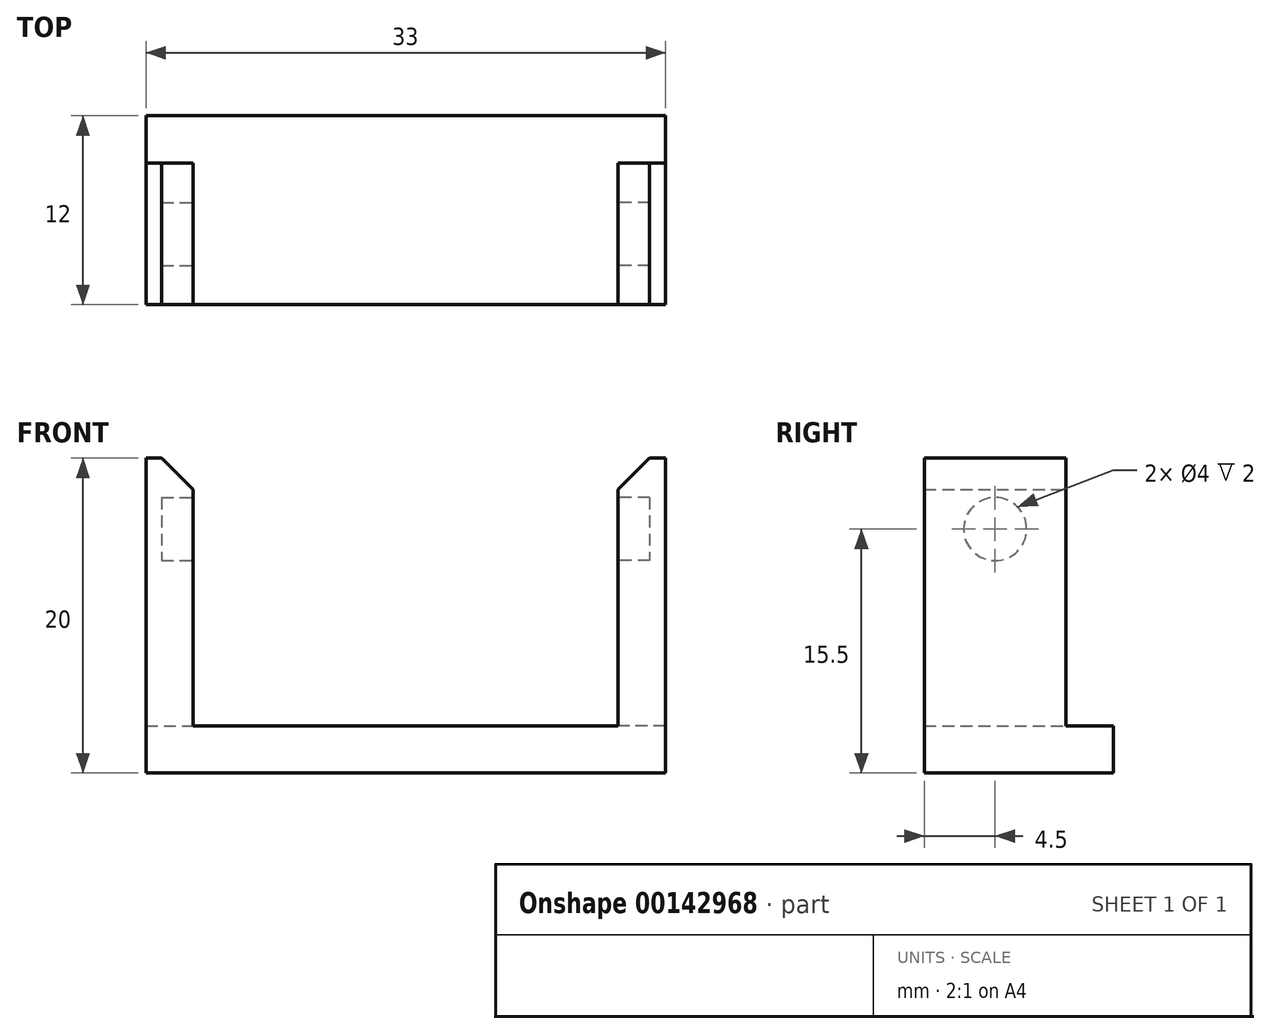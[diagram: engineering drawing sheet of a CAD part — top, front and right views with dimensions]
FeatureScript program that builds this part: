
annotation { "Feature Type Name" : "Feature", "Feature Type Description" : "" }
export const myFeature = defineFeature(function(context is Context, id is Id, definition is map)
    precondition{}
    {
        {
            var Q0;
            Q0=qCreatedBy(makeId("Top.planeOp"),FACE);
            var sketch = newSketch(context, id + "F0", { "sketchPlane" : qUnion([Q0])});
            skLineSegment(sketch, "E0.bottom", {"start": v(16.5, -6) * mm, "end": v(-16.5, -6) * mm});
            skLineSegment(sketch, "E0.top", {"start": v(16.5, 6) * mm, "end": v(-16.5, 6) * mm});
            skLineSegment(sketch, "E0.left", {"start": v(16.5, -6) * mm, "end": v(16.5, 6) * mm});
            skLineSegment(sketch, "E0.right", {"start": v(-16.5, -6) * mm, "end": v(-16.5, 6) * mm});
            skPoint(sketch, "E0.middle", {"position": v(0, 0) * mm});
            skSolve(sketch);
        }
        {
            var Q0;
            Q0 = qSketchRegion(id + "F0", true);
            extrude(context, id + "F1", {"entities" : qUnion([Q0]), "depth" : 3 * mm});
        }
        {
            var Q0;
            Q0=makeQuery(id+"F1.opExtrude","CAP_FACE",FACE,{"disambiguationData":[OSD([sQuery(id+"F0.wireOp",EDGE,"E0.bottom"),sQuery(id+"F0.wireOp",EDGE,"E0.top"),sQuery(id+"F0.wireOp",EDGE,"E0.left"),sQuery(id+"F0.wireOp",EDGE,"E0.right")])],"isStart":false});
            var sketch = newSketch(context, id + "F2", { "sketchPlane" : qUnion([Q0])});
            skLineSegment(sketch, "E1.bottom", {"start": v(16.5, -6) * mm, "end": v(13.5, -6) * mm});
            skLineSegment(sketch, "E1.top", {"start": v(16.5, 3) * mm, "end": v(13.5, 3) * mm});
            skLineSegment(sketch, "E1.left", {"start": v(16.5, -6) * mm, "end": v(16.5, 3) * mm});
            skLineSegment(sketch, "E1.right", {"start": v(13.5, -6) * mm, "end": v(13.5, 3) * mm});
            skSolve(sketch);
        }
        {
            var Q0;
            Q0 = qSketchRegion(id + "F2", true);
            extrude(context, id + "F3", {"entities" : qUnion([Q0]), "depth" : 17 * mm});
        }
        {
            var Q0;
            Q0=makeQuery(id+"F3.opExtrude","SWEPT_FACE",FACE,{"disambiguationData":[OSD([sQuery(id+"F2.wireOp",EDGE,"E1.right")])]});
            var sketch = newSketch(context, id + "F4", { "sketchPlane" : qUnion([Q0])});
            skLineSegment(sketch, "E2.0", {"start": v(6, 20) * mm, "end": v(6, 3) * mm});
            skLineSegment(sketch, "E2.1", {"start": v(6, 20) * mm, "end": v(-3, 20) * mm});
            skCircle(sketch, "E3", {"center": v(1.5, 15.5) * mm, "radius": 2 * mm});
            skSolve(sketch);
        }
        {
            var Q0;
            Q0 = qSketchRegion(id + "F4", true);
            extrude(context, id + "F5", {"entities" : qUnion([Q0]), "operationType" : NewBodyOperationType.REMOVE, "oppositeDirection" : true, "depth" : 2 * mm});
        }
        {
            var Q0;
            Q0=makeQuery(id+"F3.opExtrude","CAP_EDGE",EDGE,{"disambiguationData":[OSD([sQuery(id+"F2.wireOp",EDGE,"E1.right")])],"isStart":false});
            chamfer(context, id + "F6", {"entities" : qUnion([Q0]), "width" : 2 * mm, "tangentPropagation" : true});
        }
        {
            var Q0;
            Q0=makeQuery(id+"F3.opExtrude","SWEPT_BODY",BODY,{"disambiguationData":[OSD([sQuery(id+"F2.wireOp",EDGE,"E1.bottom"),sQuery(id+"F2.wireOp",EDGE,"E1.top"),sQuery(id+"F2.wireOp",EDGE,"E1.left"),sQuery(id+"F2.wireOp",EDGE,"E1.right")])]});
            var Q1;
            Q1=qCreatedBy(makeId("Right.planeOp"),FACE);
            mirror(context, id + "F7", {"operationType" : NewBodyOperationType.ADD, "entities" : qUnion([Q0]), "mirrorPlane" : qUnion([Q1])});
        }
    });
